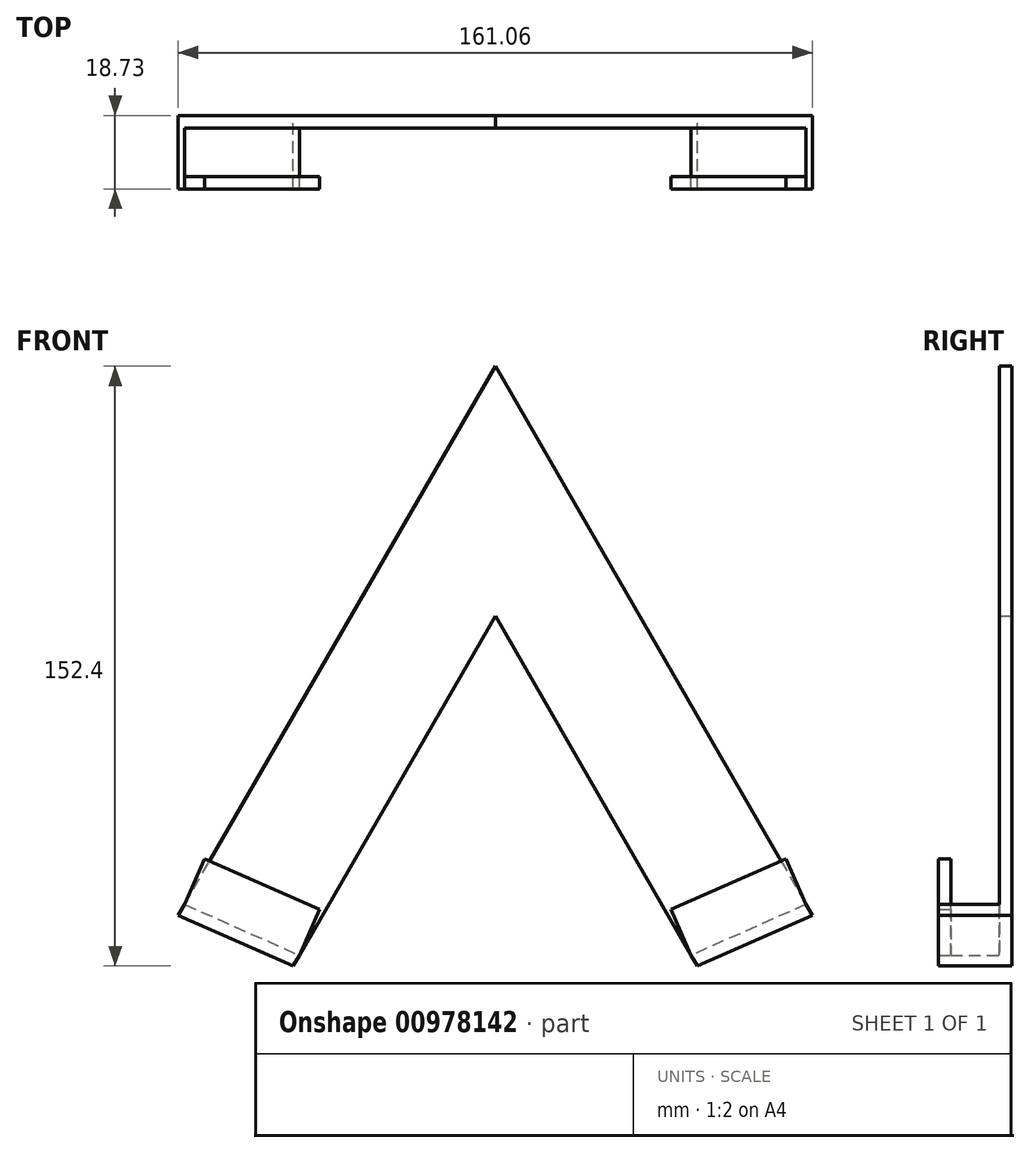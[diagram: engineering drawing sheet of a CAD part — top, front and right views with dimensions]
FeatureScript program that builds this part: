
annotation { "Feature Type Name" : "Feature", "Feature Type Description" : "" }
export const myFeature = defineFeature(function(context is Context, id is Id, definition is map)
    precondition{}
    {
        {
            var Q0;
            Q0=qCreatedBy(makeId("Front.planeOp"),FACE);
            var sketch = newSketch(context, id + "F0", { "sketchPlane" : qUnion([Q0])});
            skLineSegment(sketch, "E0", {"start": v(0, 0) * mm, "end": v(-51.33, -88.9) * mm});
            skLineSegment(sketch, "E1", {"start": v(-80.53, -75.97) * mm, "end": v(0, 63.5) * mm});
            skLineSegment(sketch, "E2", {"start": v(0, 63.5) * mm, "end": v(80.53, -75.97) * mm});
            skLineSegment(sketch, "E3", {"start": v(51.33, -88.9) * mm, "end": v(0, 0) * mm});
            skLineSegment(sketch, "E4", {"start": v(-51.33, -88.9) * mm, "end": v(0, -88.9) * mm, "construction": true});
            skLineSegment(sketch, "E5", {"start": v(0, -88.9) * mm, "end": v(51.33, -88.9) * mm, "construction": true});
            skLineSegment(sketch, "E6", {"start": v(-80.53, -75.97) * mm, "end": v(-51.33, -88.9) * mm});
            skLineSegment(sketch, "E7", {"start": v(80.53, -75.97) * mm, "end": v(51.33, -88.9) * mm});
            skLineSegment(sketch, "E8", {"start": v(0, 0) * mm, "end": v(0, 63.5) * mm});
            skSolve(sketch);
        }
        {
            var Q0;
            Q0 = qSketchRegion(id + "F0", true);
            extrude(context, id + "F1", {"entities" : qUnion([Q0]), "depth" : 3.17 * mm, "offsetDistance" : 25.4 * mm});
        }
        {
            var Q0;
            Q0=makeQuery(id+"F1.opExtrude","CAP_FACE",FACE,{"disambiguationData":[OSD([sQuery(id+"F0.wireOp",EDGE,"E0"),sQuery(id+"F0.wireOp",EDGE,"E1"),sQuery(id+"F0.wireOp",EDGE,"E2"),sQuery(id+"F0.wireOp",EDGE,"E3"),sQuery(id+"F0.wireOp",EDGE,"E6"),sQuery(id+"F0.wireOp",EDGE,"E7")])],"isStart":false});
            var sketch = newSketch(context, id + "F2", { "sketchPlane" : qUnion([Q0])});
            skLineSegment(sketch, "E9", {"start": v(-80.53, -75.97) * mm, "end": v(-78.94, -73.22) * mm});
            skLineSegment(sketch, "E10", {"start": v(-78.94, -73.22) * mm, "end": v(-49.74, -86.15) * mm});
            skLineSegment(sketch, "E11", {"start": v(-49.74, -86.15) * mm, "end": v(-51.33, -88.9) * mm});
            skLineSegment(sketch, "E12", {"start": v(-51.33, -88.9) * mm, "end": v(-80.53, -75.97) * mm});
            skLineSegment(sketch, "E13", {"start": v(51.33, -88.9) * mm, "end": v(80.53, -75.97) * mm});
            skLineSegment(sketch, "E14", {"start": v(80.53, -75.97) * mm, "end": v(78.94, -73.22) * mm});
            skLineSegment(sketch, "E15", {"start": v(78.94, -73.22) * mm, "end": v(49.74, -86.15) * mm});
            skLineSegment(sketch, "E16", {"start": v(49.74, -86.15) * mm, "end": v(51.33, -88.9) * mm});
            skSolve(sketch);
        }
        {
            var Q0;
            Q0 = qSketchRegion(id + "F2", true);
            extrude(context, id + "F3", {"entities" : qUnion([Q0]), "operationType" : NewBodyOperationType.ADD, "depth" : 15.56 * mm, "offsetDistance" : 25.4 * mm});
        }
        {
            var Q0;
            Q0=makeQuery(id+"F3.opExtrude","SWEPT_FACE",FACE,{"disambiguationData":[OSD([sQuery(id+"F2.wireOp",EDGE,"E10")])]});
            var sketch = newSketch(context, id + "F4", { "sketchPlane" : qUnion([Q0])});
            skLineSegment(sketch, "E17", {"start": v(-10.6, -18.73) * mm, "end": v(-10.6, -15.56) * mm});
            skLineSegment(sketch, "E18", {"start": v(-10.6, -15.56) * mm, "end": v(-42.54, -15.56) * mm});
            skLineSegment(sketch, "E19", {"start": v(-42.54, -15.56) * mm, "end": v(-42.54, -18.73) * mm});
            skLineSegment(sketch, "E20", {"start": v(-42.54, -18.73) * mm, "end": v(-10.6, -18.73) * mm});
            skSolve(sketch);
        }
        {
            var Q0;
            Q0 = qSketchRegion(id + "F4", true);
            extrude(context, id + "F5", {"entities" : qUnion([Q0]), "operationType" : NewBodyOperationType.ADD, "depth" : 12.7 * mm, "offsetDistance" : 25.4 * mm});
        }
        {
            var Q0;
            Q0=makeQuery(id+"F3.opExtrude","SWEPT_FACE",FACE,{"disambiguationData":[OSD([sQuery(id+"F2.wireOp",EDGE,"E15")])]});
            var sketch = newSketch(context, id + "F6", { "sketchPlane" : qUnion([Q0])});
            skLineSegment(sketch, "E21", {"start": v(10.6, -15.56) * mm, "end": v(42.54, -15.56) * mm});
            skLineSegment(sketch, "E22", {"start": v(42.54, -15.56) * mm, "end": v(42.54, -18.73) * mm});
            skLineSegment(sketch, "E23", {"start": v(42.54, -18.73) * mm, "end": v(10.6, -18.73) * mm});
            skLineSegment(sketch, "E24", {"start": v(10.6, -18.73) * mm, "end": v(10.6, -15.56) * mm});
            skSolve(sketch);
        }
        {
            var Q0;
            Q0 = qSketchRegion(id + "F6", true);
            extrude(context, id + "F7", {"entities" : qUnion([Q0]), "operationType" : NewBodyOperationType.ADD, "depth" : 12.7 * mm, "offsetDistance" : 25.4 * mm});
        }
    });
